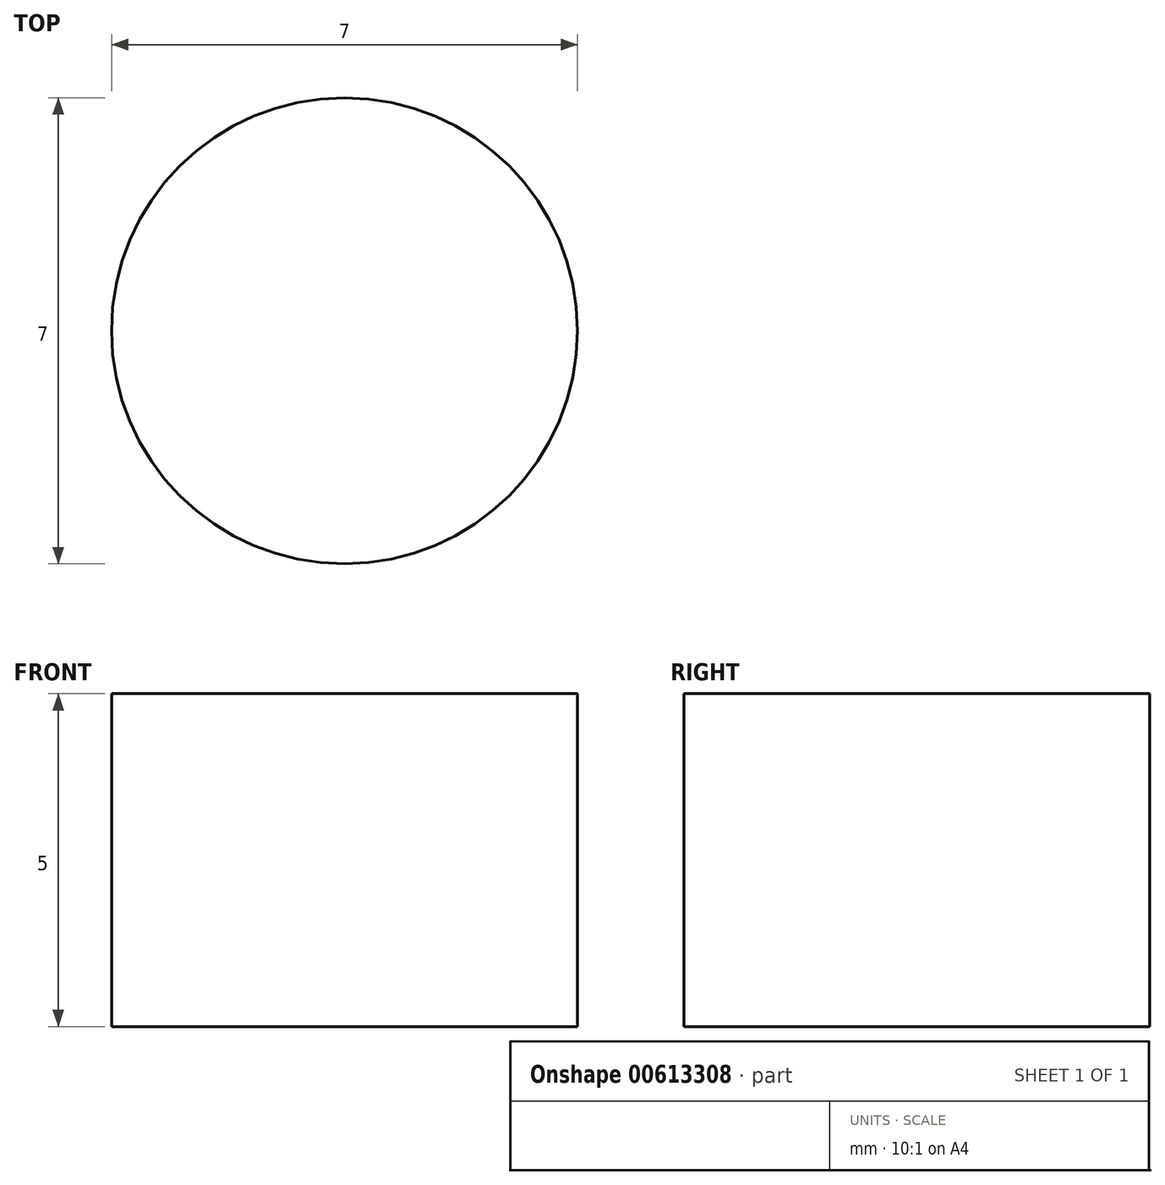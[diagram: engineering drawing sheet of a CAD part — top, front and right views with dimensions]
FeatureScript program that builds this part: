
annotation { "Feature Type Name" : "Feature", "Feature Type Description" : "" }
export const myFeature = defineFeature(function(context is Context, id is Id, definition is map)
    precondition{}
    {
        {
            var Q0;
            Q0=qCreatedBy(makeId("Top.planeOp"),FACE);
            var sketch = newSketch(context, id + "F0", { "sketchPlane" : qUnion([Q0])});
            skCircle(sketch, "E0", {"center": v(0, 0) * mm, "radius": 3.5 * mm});
            skSolve(sketch);
        }
        {
            var Q0;
            Q0 = qSketchRegion(id + "F0", true);
            extrude(context, id + "F1", {"entities" : qUnion([Q0]), "depth" : 5 * mm, "offsetDistance" : 25 * mm});
        }
    });
